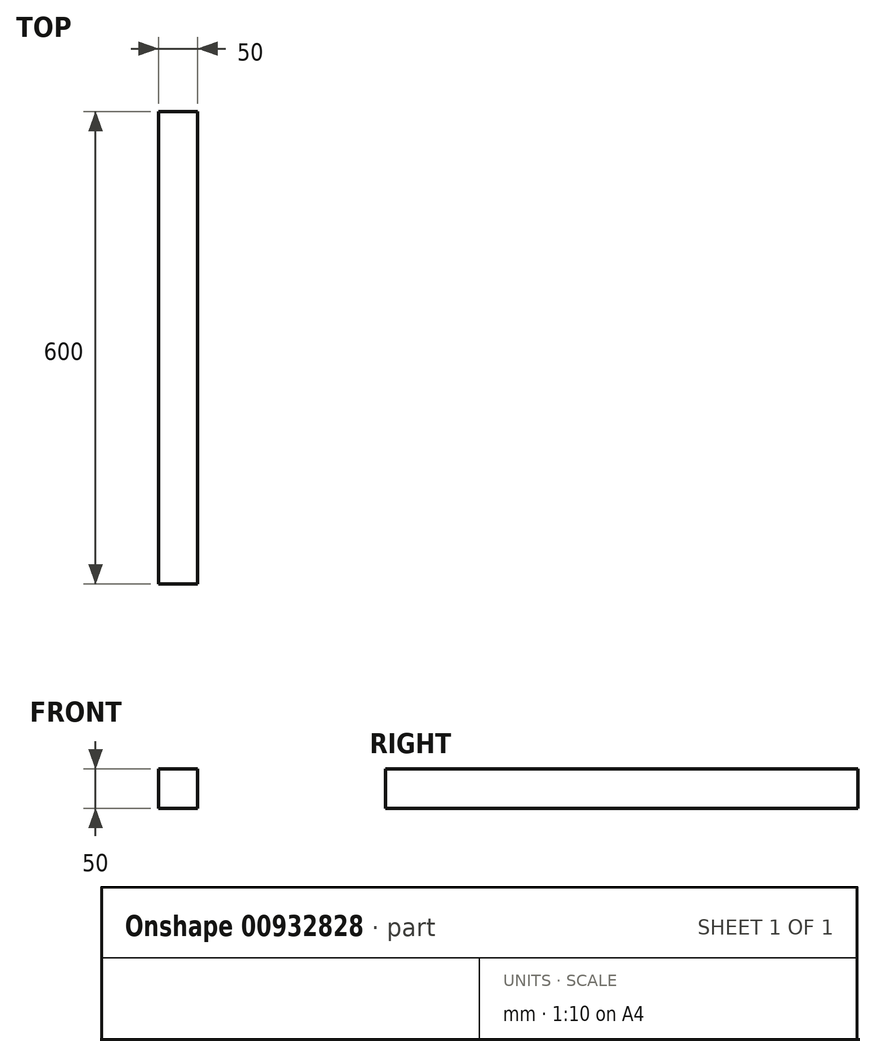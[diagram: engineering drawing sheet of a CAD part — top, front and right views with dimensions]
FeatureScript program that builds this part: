
annotation { "Feature Type Name" : "Feature", "Feature Type Description" : "" }
export const myFeature = defineFeature(function(context is Context, id is Id, definition is map)
    precondition{}
    {
        {
            var Q0;
            Q0=qCreatedBy(makeId("Front.planeOp"),FACE);
            var sketch = newSketch(context, id + "F0", { "sketchPlane" : qUnion([Q0])});
            skLineSegment(sketch, "E0.bottom", {"start": v(25, 25) * mm, "end": v(-25, 25) * mm});
            skLineSegment(sketch, "E0.top", {"start": v(25, -25) * mm, "end": v(-25, -25) * mm});
            skLineSegment(sketch, "E0.left", {"start": v(25, 25) * mm, "end": v(25, -25) * mm});
            skLineSegment(sketch, "E0.right", {"start": v(-25, 25) * mm, "end": v(-25, -25) * mm});
            skPoint(sketch, "E0.middle", {"position": v(0, 0) * mm});
            skSolve(sketch);
        }
        {
            var Q0;
            Q0 = qSketchRegion(id + "F0", true);
            extrude(context, id + "F1", {"entities" : qUnion([Q0]), "depth" : 600 * mm, "offsetDistance" : 25 * mm, "symmetric" : true});
        }
    });
